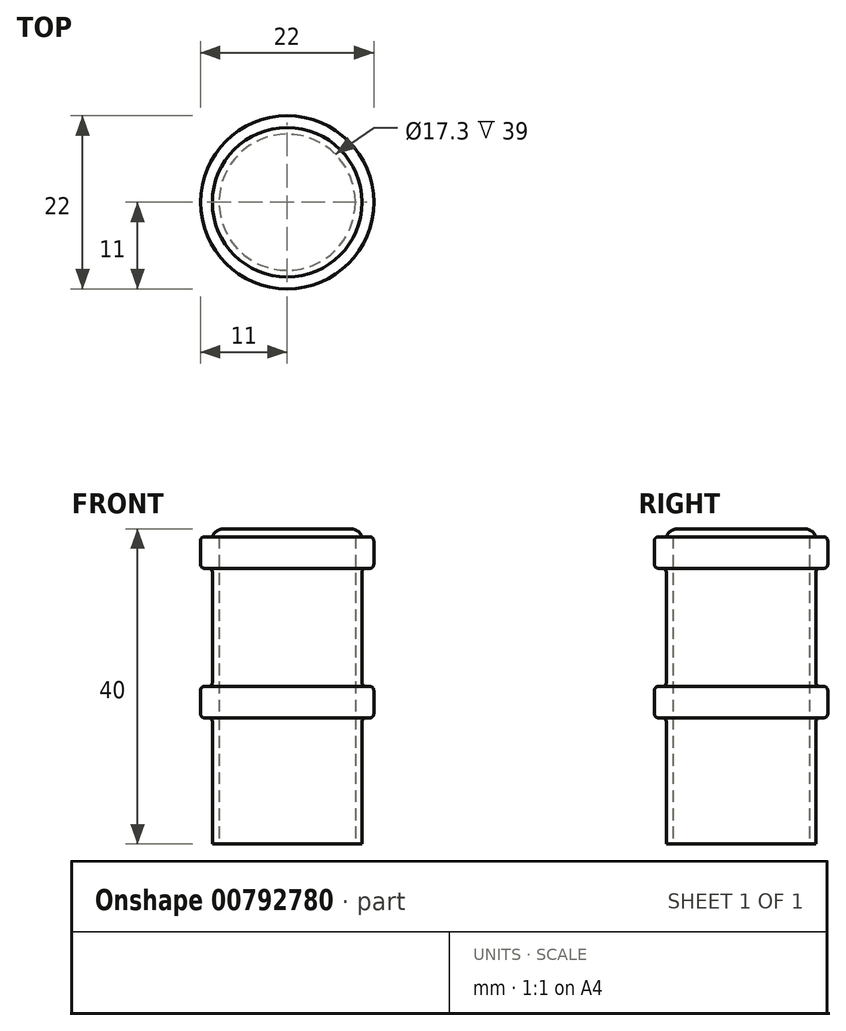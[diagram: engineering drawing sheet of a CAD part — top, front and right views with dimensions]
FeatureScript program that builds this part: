
annotation { "Feature Type Name" : "Feature", "Feature Type Description" : "" }
export const myFeature = defineFeature(function(context is Context, id is Id, definition is map)
    precondition{}
    {
        {
            var Q0;
            Q0=qCreatedBy(makeId("Top.planeOp"),FACE);
            var sketch = newSketch(context, id + "F0", { "sketchPlane" : qUnion([Q0])});
            skCircle(sketch, "E0", {"center": v(0, 0) * mm, "radius": 9.5 * mm});
            skSolve(sketch);
        }
        {
            var Q0;
            Q0 = qSketchRegion(id + "F0", true);
            extrude(context, id + "F1", {"entities" : qUnion([Q0]), "depth" : 40 * mm, "offsetDistance" : 25 * mm});
        }
        {
            var Q0;
            Q0=makeQuery(id+"F1.opExtrude","CAP_FACE",FACE,{"disambiguationData":[OSD([sQuery(id+"F0.wireOp",EDGE,"E0")])],"isStart":true});
            var sketch = newSketch(context, id + "F2", { "sketchPlane" : qUnion([Q0])});
            skCircle(sketch, "E1", {"center": v(0, 0) * mm, "radius": 8.65 * mm});
            skSolve(sketch);
        }
        {
            var Q0;
            Q0 = qSketchRegion(id + "F2", true);
            extrude(context, id + "F3", {"entities" : qUnion([Q0]), "operationType" : NewBodyOperationType.REMOVE, "oppositeDirection" : true, "depth" : 37.5 * mm, "offsetDistance" : 25 * mm});
        }
        {
            var Q0;
            Q0=makeQuery(id+"F1.opExtrude","CAP_FACE",FACE,{"disambiguationData":[OSD([sQuery(id+"F0.wireOp",EDGE,"E0")])],"isStart":false});
            cPlane(context, id + "F4", {"entities" : qUnion([Q0]), "cplaneType" : CPlaneType.OFFSET, "offset" : 1 * mm, "oppositeDirection" : true, "width" : 150 * mm, "height" : 150 * mm});
        }
        {
            var Q0;
            Q0=qCreatedBy(id+"F4.planeOp",FACE);
            var sketch = newSketch(context, id + "F5", { "sketchPlane" : qUnion([Q0])});
            skCircle(sketch, "E2", {"center": v(0, 0) * mm, "radius": 11 * mm});
            skSolve(sketch);
        }
        {
            var Q0;
            Q0 = qSketchRegion(id + "F5", true);
            extrude(context, id + "F6", {"entities" : qUnion([Q0]), "operationType" : NewBodyOperationType.ADD, "oppositeDirection" : true, "depth" : 4 * mm, "offsetDistance" : 25 * mm});
        }
        {
            var Q0;
            Q0=qCreatedBy(id+"F4.planeOp",FACE);
            cPlane(context, id + "F7", {"entities" : qUnion([Q0]), "cplaneType" : CPlaneType.OFFSET, "offset" : 19 * mm, "oppositeDirection" : true, "width" : 150 * mm, "height" : 150 * mm});
        }
        {
            var Q0;
            Q0=qCreatedBy(id+"F7.planeOp",FACE);
            var sketch = newSketch(context, id + "F8", { "sketchPlane" : qUnion([Q0])});
            skCircle(sketch, "E3", {"center": v(0, 0) * mm, "radius": 11 * mm});
            skSolve(sketch);
        }
        {
            var Q0;
            Q0 = qSketchRegion(id + "F8", true);
            extrude(context, id + "F9", {"entities" : qUnion([Q0]), "operationType" : NewBodyOperationType.ADD, "oppositeDirection" : true, "depth" : 4 * mm, "offsetDistance" : 25 * mm});
        }
        {
            var Q0;
            Q0=makeQuery(id+"F1.opExtrude","CAP_EDGE",EDGE,{"disambiguationData":[OSD([sQuery(id+"F0.wireOp",EDGE,"E0")])],"isStart":false});
            fillet(context, id + "F10", {"entities" : qUnion([Q0]), "radius" : 1.5 * mm, "tangentPropagation" : true, "allowEdgeOverflow" : false});
        }
        {
            var Q0;
            Q0=makeQuery(id+"F6.opExtrude","SWEPT_FACE",FACE,{"disambiguationData":[OSD([sQuery(id+"F5.wireOp",EDGE,"E2")])]});
            fillet(context, id + "F11", {"entities" : qUnion([Q0]), "radius" : 0.5 * mm, "tangentPropagation" : true, "allowEdgeOverflow" : false});
        }
        {
            var Q0;
            Q0=makeQuery(id+"F6.boolean.opBoolean","INTERSECT",EDGE,{"derivedFrom":[makeQuery(id+"F1.opExtrude","SWEPT_FACE",FACE,{"disambiguationData":[OSD([sQuery(id+"F0.wireOp",EDGE,"E0")])]}),makeQuery(id+"F6.opExtrude","CAP_FACE",FACE,{"disambiguationData":[OSD([sQuery(id+"F5.wireOp",EDGE,"E2")])],"isStart":false})]});
            fillet(context, id + "F12", {"entities" : qUnion([Q0]), "radius" : 0.5 * mm, "tangentPropagation" : true, "allowEdgeOverflow" : false});
        }
        {
            var Q0;
            Q0=makeQuery(id+"F9.opExtrude","SWEPT_FACE",FACE,{"disambiguationData":[OSD([sQuery(id+"F8.wireOp",EDGE,"E3")])]});
            fillet(context, id + "F13", {"entities" : qUnion([Q0]), "radius" : 0.5 * mm, "tangentPropagation" : true, "allowEdgeOverflow" : false});
        }
        {
            var Q0;
            {var subQ0=sQuery(id+"F0.wireOp",EDGE,"E0");Q0=makeQuery(id+"F9.boolean.opBoolean","INTERSECT",EDGE,{"derivedFrom":[makeQuery(id+"F6.boolean.opBoolean","SPLIT",FACE,{"disambiguationData":[TD([makeQuery(id+"F1.opExtrude","CAP_FACE",FACE,{"disambiguationData":[OSD([subQ0])],"isStart":true})])],"derivedFrom":makeQuery(id+"F1.opExtrude","SWEPT_FACE",FACE,{"disambiguationData":[OSD([subQ0])]})}),makeQuery(id+"F9.opExtrude","CAP_FACE",FACE,{"disambiguationData":[OSD([sQuery(id+"F8.wireOp",EDGE,"E3")])],"isStart":true})]});}
            fillet(context, id + "F14", {"entities" : qUnion([Q0]), "radius" : 0.5 * mm, "tangentPropagation" : true, "allowEdgeOverflow" : false});
        }
        {
            var Q0;
            {var subQ0=sQuery(id+"F0.wireOp",EDGE,"E0");Q0=makeQuery(id+"F9.boolean.opBoolean","INTERSECT",EDGE,{"derivedFrom":[makeQuery(id+"F6.boolean.opBoolean","SPLIT",FACE,{"disambiguationData":[TD([makeQuery(id+"F1.opExtrude","CAP_FACE",FACE,{"disambiguationData":[OSD([subQ0])],"isStart":true})])],"derivedFrom":makeQuery(id+"F1.opExtrude","SWEPT_FACE",FACE,{"disambiguationData":[OSD([subQ0])]})}),makeQuery(id+"F9.opExtrude","CAP_FACE",FACE,{"disambiguationData":[OSD([sQuery(id+"F8.wireOp",EDGE,"E3")])],"isStart":false})]});}
            fillet(context, id + "F15", {"entities" : qUnion([Q0]), "radius" : 0.5 * mm, "tangentPropagation" : true, "allowEdgeOverflow" : false});
        }
        {
            var Q0;
            Q0=makeQuery(id+"F1.opExtrude","CAP_FACE",FACE,{"disambiguationData":[OSD([sQuery(id+"F0.wireOp",EDGE,"E0")])],"isStart":true});
            var sketch = newSketch(context, id + "F16", { "sketchPlane" : qUnion([Q0])});
            skCircle(sketch, "E4", {"center": v(0, 0) * mm, "radius": 8.65 * mm});
            skSolve(sketch);
        }
        {
            var Q0;
            Q0 = qSketchRegion(id + "F16", true);
            extrude(context, id + "F17", {"entities" : qUnion([Q0]), "operationType" : NewBodyOperationType.REMOVE, "oppositeDirection" : true, "depth" : 39 * mm, "offsetDistance" : 25 * mm});
        }
        {
            var Q0;
            Q0=makeQuery(id+"F17.boolean.opBoolean","COPY",FACE,{"derivedFrom":makeQuery(id+"F17.opExtrude","CAP_FACE",FACE,{"disambiguationData":[OSD([sQuery(id+"F16.wireOp",EDGE,"E4")])],"isStart":false})});
            cPlane(context, id + "F18", {"entities" : qUnion([Q0]), "cplaneType" : CPlaneType.OFFSET, "offset" : 10.8 * mm, "width" : 150 * mm, "height" : 150 * mm});
        }
    });
